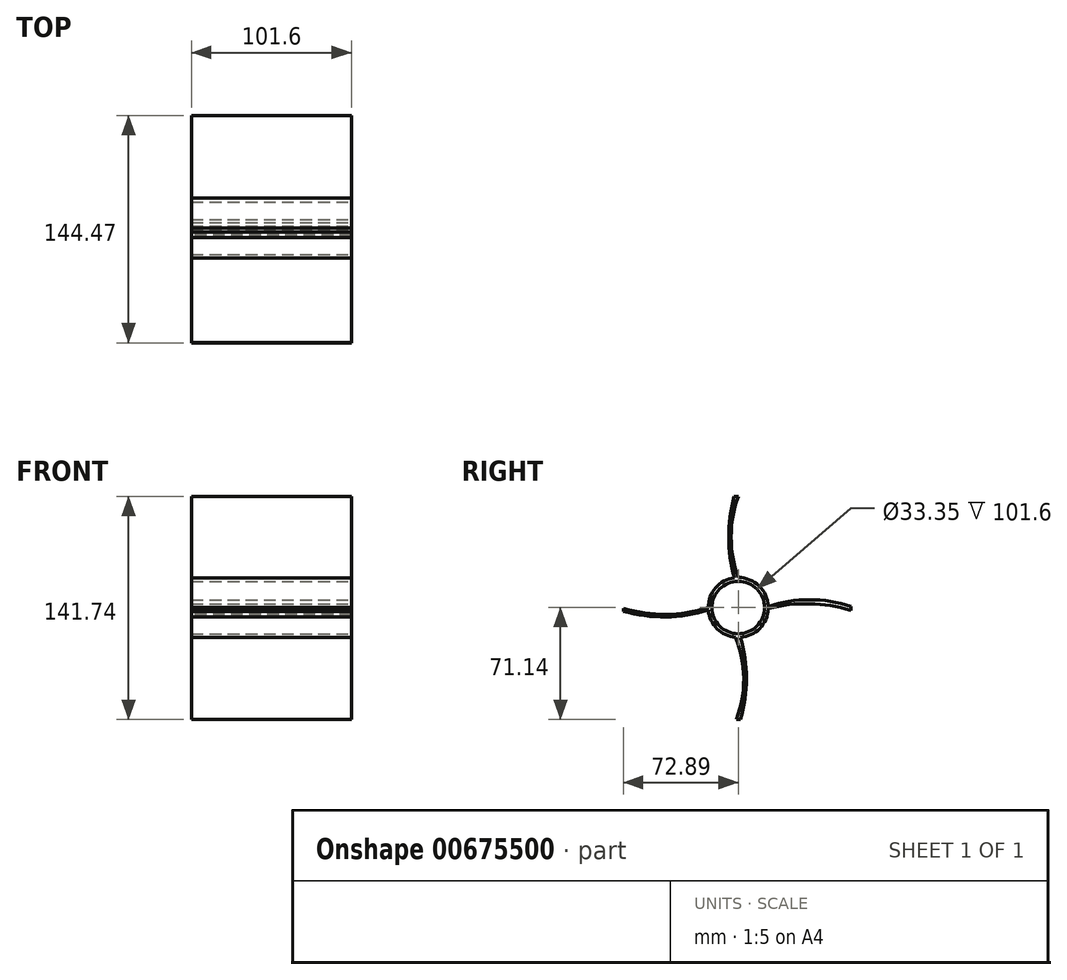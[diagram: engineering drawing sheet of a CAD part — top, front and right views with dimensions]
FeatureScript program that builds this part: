
annotation { "Feature Type Name" : "Feature", "Feature Type Description" : "" }
export const myFeature = defineFeature(function(context is Context, id is Id, definition is map)
    precondition{}
    {
        {
            var Q0;
            Q0=qCreatedBy(makeId("Right.planeOp"),FACE);
            var sketch = newSketch(context, id + "F0", { "sketchPlane" : qUnion([Q0])});
            skCircle(sketch, "E0", {"center": v(0, 0) * mm, "radius": 19.05 * mm});
            skSolve(sketch);
        }
        {
            var Q0;
            Q0 = qSketchRegion(id + "F0", true);
            extrude(context, id + "F1", {"entities" : qUnion([Q0]), "depth" : 101.6 * mm, "offsetDistance" : 25.4 * mm});
        }
        {
            var Q0;
            Q0=makeQuery(id+"F1.opExtrude","CAP_FACE",FACE,{"disambiguationData":[OSD([sQuery(id+"F0.wireOp",EDGE,"E0")])],"isStart":false});
            var sketch = newSketch(context, id + "F2", { "sketchPlane" : qUnion([Q0])});
            skCircle(sketch, "E1", {"center": v(0, 0) * mm, "radius": 16.67 * mm});
            skSolve(sketch);
        }
        {
            var Q0;
            Q0 = qSketchRegion(id + "F2", true);
            extrude(context, id + "F3", {"entities" : qUnion([Q0]), "operationType" : NewBodyOperationType.REMOVE, "oppositeDirection" : true, "depth" : 101.6 * mm, "offsetDistance" : 25.4 * mm});
        }
        {
            var Q0;
            Q0=makeQuery(id+"F1.opExtrude","CAP_FACE",FACE,{"disambiguationData":[OSD([sQuery(id+"F0.wireOp",EDGE,"E0")])],"isStart":true});
            var sketch = newSketch(context, id + "F4", { "sketchPlane" : qUnion([Q0])});
            skArc(sketch, "E2", {"start": v(2.56, 18.88) * mm, "mid": v(6, 44.67) * mm, "end": v(2.62, 70.46) * mm});
            skArc(sketch, "E3", {"start": v(0, 19.05) * mm, "mid": v(4.5, 44.82) * mm, "end": v(0, 70.6) * mm});
            skLineSegment(sketch, "E4", {"start": v(0, 70.6) * mm, "end": v(2.62, 70.46) * mm});
            skLineSegment(sketch, "E5", {"start": v(2.56, 18.88) * mm, "end": v(0, 19.05) * mm});
            skSolve(sketch);
        }
        {
            var Q0;
            Q0 = qSketchRegion(id + "F4", true);
            extrude(context, id + "F5", {"entities" : qUnion([Q0]), "operationType" : NewBodyOperationType.ADD, "oppositeDirection" : true, "depth" : 101.6 * mm, "offsetDistance" : 25.4 * mm});
        }
        {
            var Q0;
            Q0=makeQuery(id+"F5.boolean.opBoolean","MERGE",FACE,{"derivedFrom":[makeQuery(id+"F1.opExtrude","CAP_FACE",FACE,{"disambiguationData":[OSD([sQuery(id+"F0.wireOp",EDGE,"E0")])],"isStart":false}),makeQuery(id+"F5.opExtrude","CAP_FACE",FACE,{"disambiguationData":[OSD([sQuery(id+"F4.wireOp",EDGE,"E2"),sQuery(id+"F4.wireOp",EDGE,"E3"),sQuery(id+"F4.wireOp",EDGE,"E4"),sQuery(id+"F4.wireOp",EDGE,"E5")])],"isStart":false})]});
            var sketch = newSketch(context, id + "F6", { "sketchPlane" : qUnion([Q0])});
            skArc(sketch, "E6", {"start": v(1.28, -71.14) * mm, "mid": v(5.28, -45.07) * mm, "end": v(1.28, -19) * mm});
            skPoint(sketch, "E6.startSnap0", {"position": v(1.28, -19) * mm});
            skArc(sketch, "E7", {"start": v(-1.24, -71.14) * mm, "mid": v(3.48, -45.03) * mm, "end": v(-1.61, -18.98) * mm});
            skLineSegment(sketch, "E8", {"start": v(1.28, -71.14) * mm, "end": v(-1.24, -71.14) * mm});
            skLineSegment(sketch, "E9", {"start": v(1.28, -19) * mm, "end": v(-1.61, -18.98) * mm});
            skSolve(sketch);
        }
        {
            var Q0;
            Q0 = qSketchRegion(id + "F6", true);
            extrude(context, id + "F7", {"entities" : qUnion([Q0]), "operationType" : NewBodyOperationType.ADD, "oppositeDirection" : true, "depth" : 101.6 * mm, "offsetDistance" : 25.4 * mm});
        }
        {
            var Q0;
            Q0=makeQuery(id+"F7.boolean.opBoolean","MERGE",FACE,{"derivedFrom":[makeQuery(id+"F5.boolean.opBoolean","MERGE",FACE,{"derivedFrom":[makeQuery(id+"F1.opExtrude","CAP_FACE",FACE,{"disambiguationData":[OSD([sQuery(id+"F0.wireOp",EDGE,"E0")])],"isStart":true}),makeQuery(id+"F5.opExtrude","CAP_FACE",FACE,{"disambiguationData":[OSD([sQuery(id+"F4.wireOp",EDGE,"E2"),sQuery(id+"F4.wireOp",EDGE,"E3"),sQuery(id+"F4.wireOp",EDGE,"E4"),sQuery(id+"F4.wireOp",EDGE,"E5")])],"isStart":true})]}),makeQuery(id+"F7.opExtrude","CAP_FACE",FACE,{"disambiguationData":[OSD([sQuery(id+"F6.wireOp",EDGE,"E6"),sQuery(id+"F6.wireOp",EDGE,"E7"),sQuery(id+"F6.wireOp",EDGE,"E8"),sQuery(id+"F6.wireOp",EDGE,"E9")])],"isStart":false})]});
            var sketch = newSketch(context, id + "F8", { "sketchPlane" : qUnion([Q0])});
            skArc(sketch, "E10", {"start": v(18.97, -1.69) * mm, "mid": v(45.88, -5.98) * mm, "end": v(72.89, -2.36) * mm});
            skArc(sketch, "E11", {"start": v(18.97, 0) * mm, "mid": v(45.82, -4.42) * mm, "end": v(72.73, -0.48) * mm});
            skPoint(sketch, "E11.endSnap0", {"position": v(19.04, -0.48) * mm});
            skLineSegment(sketch, "E12", {"start": v(18.97, 0) * mm, "end": v(18.97, -1.69) * mm});
            skLineSegment(sketch, "E13", {"start": v(72.73, -0.48) * mm, "end": v(72.89, -2.36) * mm});
            skSolve(sketch);
        }
        {
            var Q0;
            Q0 = qSketchRegion(id + "F8", true);
            extrude(context, id + "F9", {"entities" : qUnion([Q0]), "operationType" : NewBodyOperationType.ADD, "oppositeDirection" : true, "depth" : 101.6 * mm, "offsetDistance" : 25.4 * mm});
        }
        {
            var Q0;
            Q0=makeQuery(id+"F9.boolean.opBoolean","MERGE",FACE,{"derivedFrom":[makeQuery(id+"F7.boolean.opBoolean","MERGE",FACE,{"derivedFrom":[makeQuery(id+"F5.boolean.opBoolean","MERGE",FACE,{"derivedFrom":[makeQuery(id+"F1.opExtrude","CAP_FACE",FACE,{"disambiguationData":[OSD([sQuery(id+"F0.wireOp",EDGE,"E0")])],"isStart":false}),makeQuery(id+"F5.opExtrude","CAP_FACE",FACE,{"disambiguationData":[OSD([sQuery(id+"F4.wireOp",EDGE,"E2"),sQuery(id+"F4.wireOp",EDGE,"E3"),sQuery(id+"F4.wireOp",EDGE,"E4"),sQuery(id+"F4.wireOp",EDGE,"E5")])],"isStart":false})]}),makeQuery(id+"F7.opExtrude","CAP_FACE",FACE,{"disambiguationData":[OSD([sQuery(id+"F6.wireOp",EDGE,"E6"),sQuery(id+"F6.wireOp",EDGE,"E7"),sQuery(id+"F6.wireOp",EDGE,"E8"),sQuery(id+"F6.wireOp",EDGE,"E9")])],"isStart":true})]}),makeQuery(id+"F9.opExtrude","CAP_FACE",FACE,{"disambiguationData":[OSD([sQuery(id+"F8.wireOp",EDGE,"E10"),sQuery(id+"F8.wireOp",EDGE,"E11"),sQuery(id+"F8.wireOp",EDGE,"E12"),sQuery(id+"F8.wireOp",EDGE,"E13")])],"isStart":false})]});
            var sketch = newSketch(context, id + "F10", { "sketchPlane" : qUnion([Q0])});
            skArc(sketch, "E14", {"start": v(71.44, -1.84) * mm, "mid": v(45.32, 2.4) * mm, "end": v(19.04, -0.64) * mm});
            skPoint(sketch, "E14.endSnap0", {"position": v(19.04, 0.64) * mm});
            skArc(sketch, "E15", {"start": v(71.58, 0.64) * mm, "mid": v(45.3, 4.93) * mm, "end": v(19.04, 0.64) * mm});
            skLineSegment(sketch, "E16", {"start": v(71.44, -1.84) * mm, "end": v(71.58, 0.64) * mm});
            skLineSegment(sketch, "E17", {"start": v(19.04, -0.64) * mm, "end": v(19.04, 0.64) * mm});
            skSolve(sketch);
        }
        {
            var Q0;
            Q0 = qSketchRegion(id + "F10", true);
            extrude(context, id + "F11", {"entities" : qUnion([Q0]), "operationType" : NewBodyOperationType.ADD, "oppositeDirection" : true, "depth" : 101.6 * mm, "offsetDistance" : 25.4 * mm});
        }
    });
